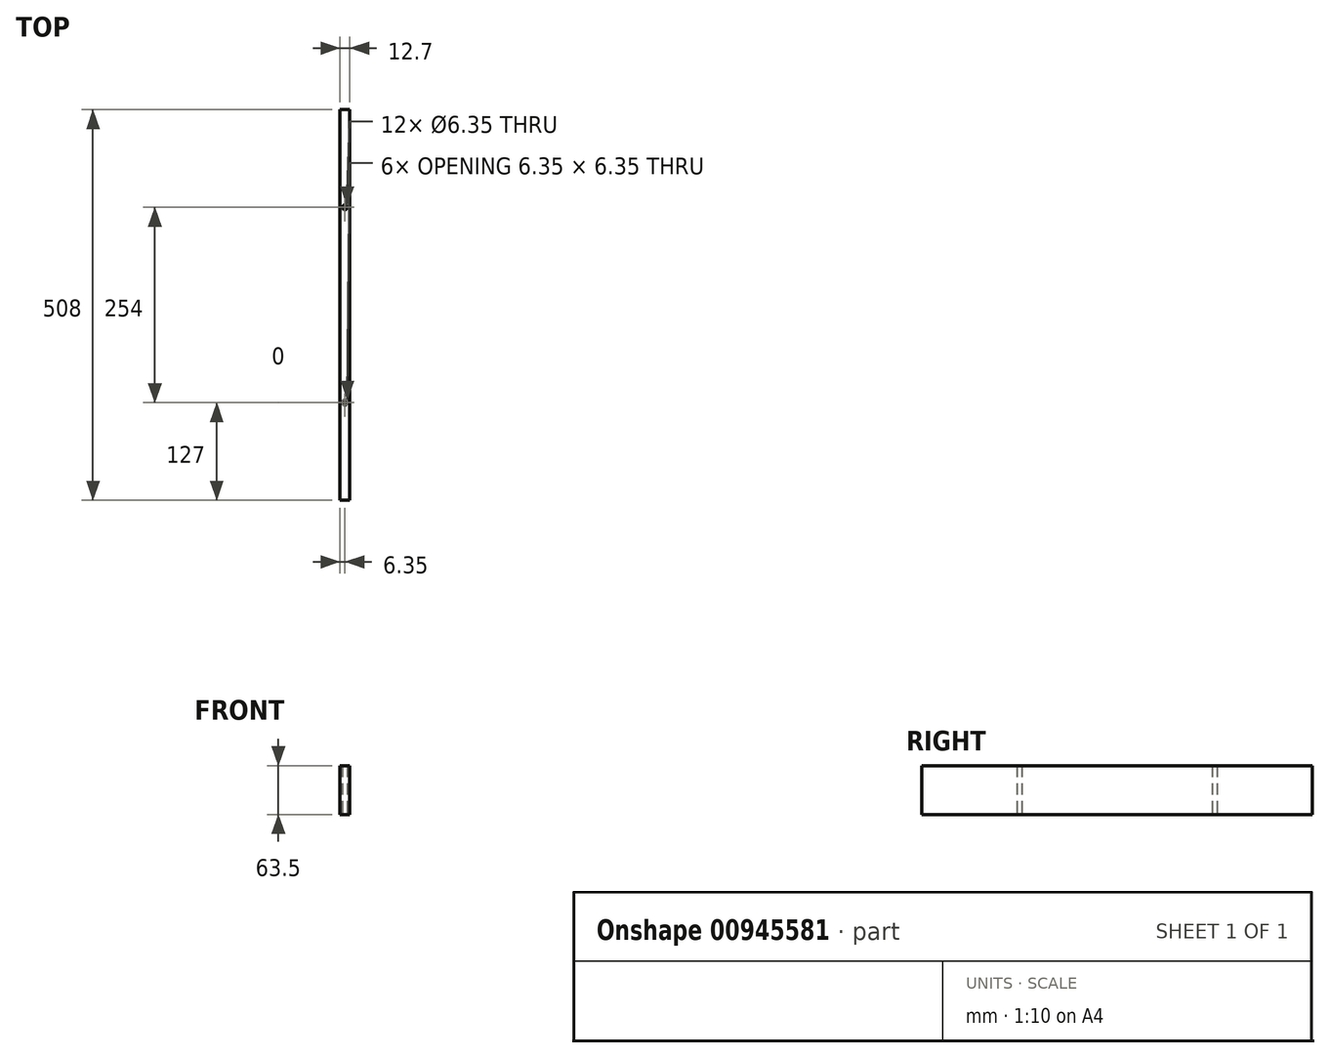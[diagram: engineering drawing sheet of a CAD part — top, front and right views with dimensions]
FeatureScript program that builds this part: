
annotation { "Feature Type Name" : "Feature", "Feature Type Description" : "" }
export const myFeature = defineFeature(function(context is Context, id is Id, definition is map)
    precondition{}
    {
        {
            var Q0;
            Q0=qCreatedBy(makeId("Top.planeOp"),FACE);
            var sketch = newSketch(context, id + "F0", { "sketchPlane" : qUnion([Q0])});
            skLineSegment(sketch, "E0.bottom", {"start": v(6.35, 254) * mm, "end": v(-6.35, 254) * mm});
            skLineSegment(sketch, "E0.top", {"start": v(6.35, -254) * mm, "end": v(-6.35, -254) * mm});
            skLineSegment(sketch, "E0.left", {"start": v(6.35, 254) * mm, "end": v(6.35, -254) * mm});
            skLineSegment(sketch, "E0.right", {"start": v(-6.35, 254) * mm, "end": v(-6.35, -254) * mm});
            skPoint(sketch, "E0.middle", {"position": v(0, 0) * mm});
            skSolve(sketch);
        }
        {
            var Q0;
            Q0=qSketchRegion(id+"F0",true);
            extrude(context, id + "F1", {"entities" : qUnion([Q0]), "depth" : 63.5 * mm, "offsetDistance" : 25 * mm});
        }
        {
            var Q0;
            Q0=makeQuery(id+"F1.opExtrude","CAP_FACE",FACE,{"disambiguationData":[OSD([sQuery(id+"F0.wireOp",EDGE,"E0.bottom"),sQuery(id+"F0.wireOp",EDGE,"E0.top"),sQuery(id+"F0.wireOp",EDGE,"E0.left"),sQuery(id+"F0.wireOp",EDGE,"E0.right")])],"isStart":true});
            var sketch = newSketch(context, id + "F2", { "sketchPlane" : qUnion([Q0])});
            skLineSegment(sketch, "E1", {"start": v(0, 254) * mm, "end": v(0, 127) * mm});
            skLineSegment(sketch, "E2", {"start": v(0, 127) * mm, "end": v(0, 0) * mm});
            skLineSegment(sketch, "E3", {"start": v(0, 0) * mm, "end": v(0, -127) * mm});
            skLineSegment(sketch, "E4", {"start": v(0, -127) * mm, "end": v(0, -254) * mm});
            skCircle(sketch, "E5", {"center": v(0, 127) * mm, "radius": 3.18 * mm});
            skCircle(sketch, "E6", {"center": v(0, -127) * mm, "radius": 3.18 * mm});
            skSolve(sketch);
        }
        {
            var Q0;
            Q0=qSketchRegion(id+"F2",true);
            var Q1;
            Q1=makeQuery(id+"F1.opExtrude","CAP_FACE",FACE,{"disambiguationData":[OSD([sQuery(id+"F0.wireOp",EDGE,"E0.bottom"),sQuery(id+"F0.wireOp",EDGE,"E0.top"),sQuery(id+"F0.wireOp",EDGE,"E0.left"),sQuery(id+"F0.wireOp",EDGE,"E0.right")])],"isStart":false});
            extrude(context, id + "F3", {"entities" : qUnion([Q0]), "operationType" : NewBodyOperationType.REMOVE, "endBound" : BoundingType.UP_TO_SURFACE, "oppositeDirection" : true, "depth" : 25 * mm, "endBoundEntityFace" : qUnion([Q1]), "offsetDistance" : 25 * mm});
        }
    });
